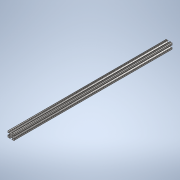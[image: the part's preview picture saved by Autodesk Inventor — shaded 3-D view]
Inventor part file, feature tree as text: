
AUTODESK INVENTOR PART (.ipt)
format: ipt  version: 2020 (Build 240168000, 168)  size: 243,200 bytes
history: native  units: in
note: dims shown in document units (in); Inventor stores cm internally (conversion verified against a paired STEP export)
features: extrude x1, sketch x1
ambient origin geometry x8: Origin, YZ Plane, XZ Plane, XY Plane, X Axis, Y Axis, Z Axis, Center Point
bodies: Solid1 (feature_tree)
feature tree (2):
  extrude  "Extrusion1"  [1 undecoded]
  sketch  "Sketch1"  dims[d0=25.0in d1=0.0in]
note: 1 required parameter value undecoded (feature->parameter linkage not recoverable at this tier; creation-order binding heuristic only, values carry confidence <= 0.55)
